# Revit family: BI-30
name_source: partatom
category: Generic Models
revit_build: Autodesk Revit LT 2016 (Build: 20161004_0715(x64)
units: mm (PartAtom-declared; Revit-internal decimal feet)

## family parameters
Always vertical = Yes
Can host rebar = No
Cut with Voids When Loaded = No
Part Type = Normal
Room Calculation Point = No
Round Connector Dimension = Use Diameter
Shared = No
Work Plane-Based = No

## types (2) — shared parameters
A = 8.882 "
B = 4.88 "
K = 3.392 "
L = 5.75 "
Manufacturer = REVERSOMATIC
URL = http://www.reversomatic.com

## per-type parameters (varying)
| type | BLADE | C | D | E | F | G | H | HOUSING | I | J | MOTOR | Model | RPM | SP/CFM |
| GPB2-130  REVERSO DESIGN | AA-326-128 | 9.75 " | 4.392 " | 7.5 " | 6.75 " | 9 " | 4.12 " | REVERSO | 37 " | 5 " | 302-5929 | GPB2-130 | 1500 | .00/127  .05/118  .10/104  .15/88  .20/72 |
| GPB2-130 BF-00 |  | 30 " | 24.5 " | 45 " | 23 " | 41 " | 32.5 " |  | 57.5 " | 53 " |  | BI-30 |  |  |

## geometry (parser evidence)
native form markers: Sweep x2
no freeform markers — native parametric forms only
